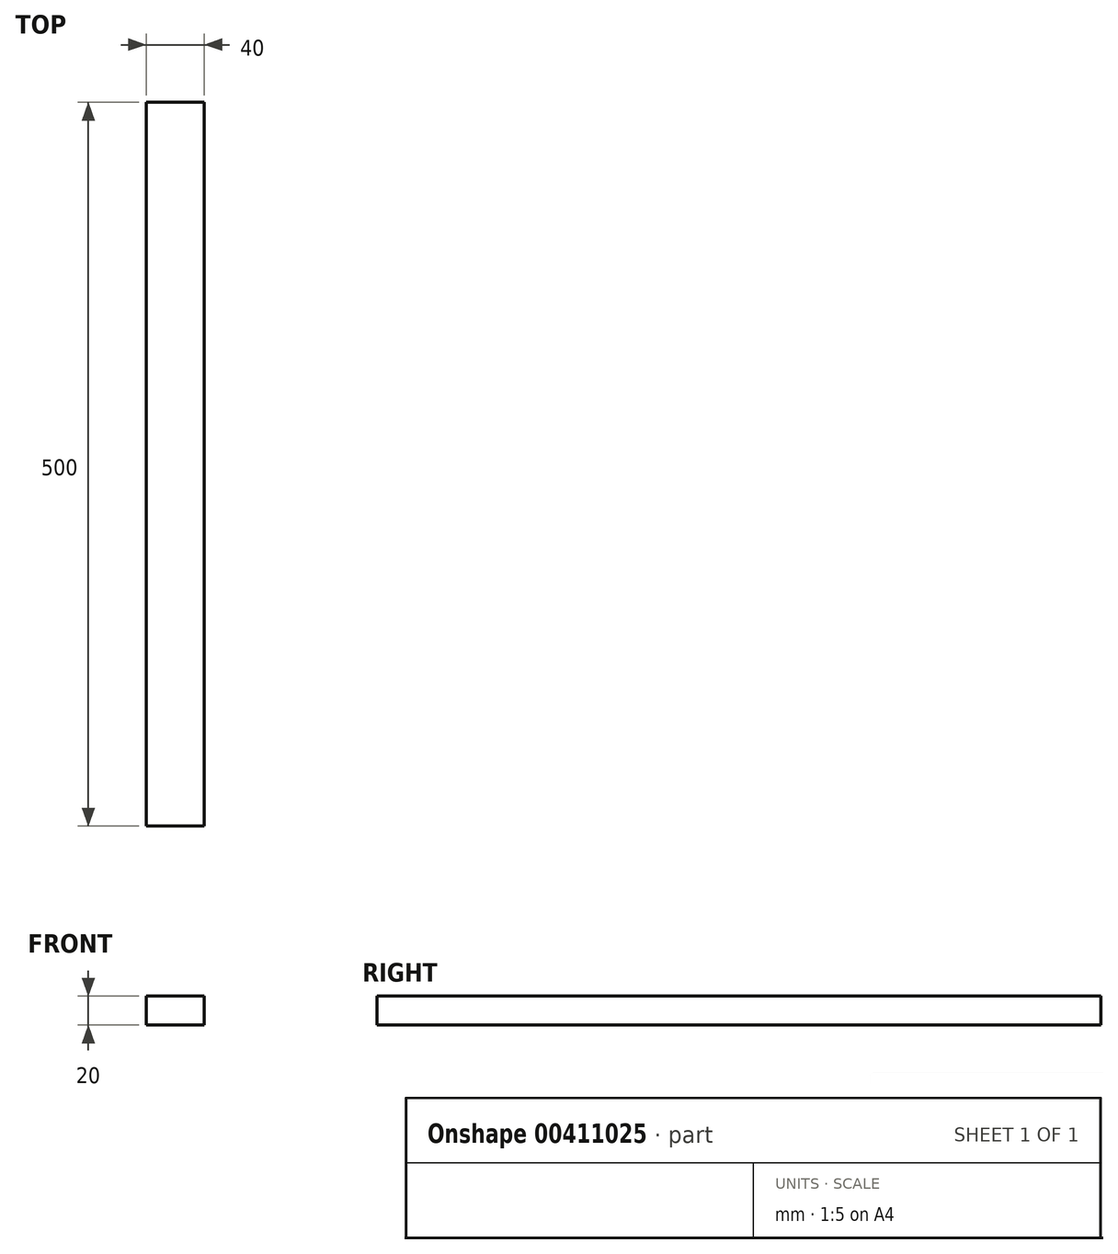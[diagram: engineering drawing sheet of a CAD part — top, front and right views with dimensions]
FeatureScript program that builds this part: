
annotation { "Feature Type Name" : "Feature", "Feature Type Description" : "" }
export const myFeature = defineFeature(function(context is Context, id is Id, definition is map)
    precondition{}
    {
        {
            var Q0;
            Q0=qCreatedBy(makeId("Front.planeOp"),FACE);
            var sketch = newSketch(context, id + "F0", { "sketchPlane" : qUnion([Q0])});
            skLineSegment(sketch, "E0.bottom", {"start": v(20, 10) * mm, "end": v(-20, 10) * mm});
            skLineSegment(sketch, "E0.top", {"start": v(20, -10) * mm, "end": v(-20, -10) * mm});
            skLineSegment(sketch, "E0.left", {"start": v(20, 10) * mm, "end": v(20, -10) * mm});
            skLineSegment(sketch, "E0.right", {"start": v(-20, 10) * mm, "end": v(-20, -10) * mm});
            skPoint(sketch, "E0.middle", {"position": v(0, 0) * mm});
            skSolve(sketch);
        }
        {
            var Q0;
            Q0 = qSketchRegion(id + "F0", true);
            extrude(context, id + "F1", {"entities" : qUnion([Q0]), "oppositeDirection" : true, "depth" : 500 * mm});
        }
    });
